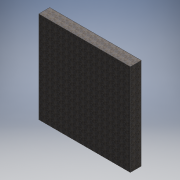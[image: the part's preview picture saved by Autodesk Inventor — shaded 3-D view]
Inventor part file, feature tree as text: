
AUTODESK INVENTOR PART (.ipt)
format: ipt  version: 2016 (Build 200138000, 138)  size: 103,424 bytes
history: native  units: mm
features: extrude x1, sketch x1
ambient origin geometry x8: Origin, YZ Plane, XZ Plane, XY Plane, X Axis, Y Axis, Z Axis, Center Point
bodies: Solid1 (feature_tree)
feature tree (2):
  extrude  "Extrusion1"  Depth=3000.0mm
  sketch  "Sketch1"  dims[d0=3000.0mm d1=3000.0mm d2=360.0mm d3=0.0mm]
